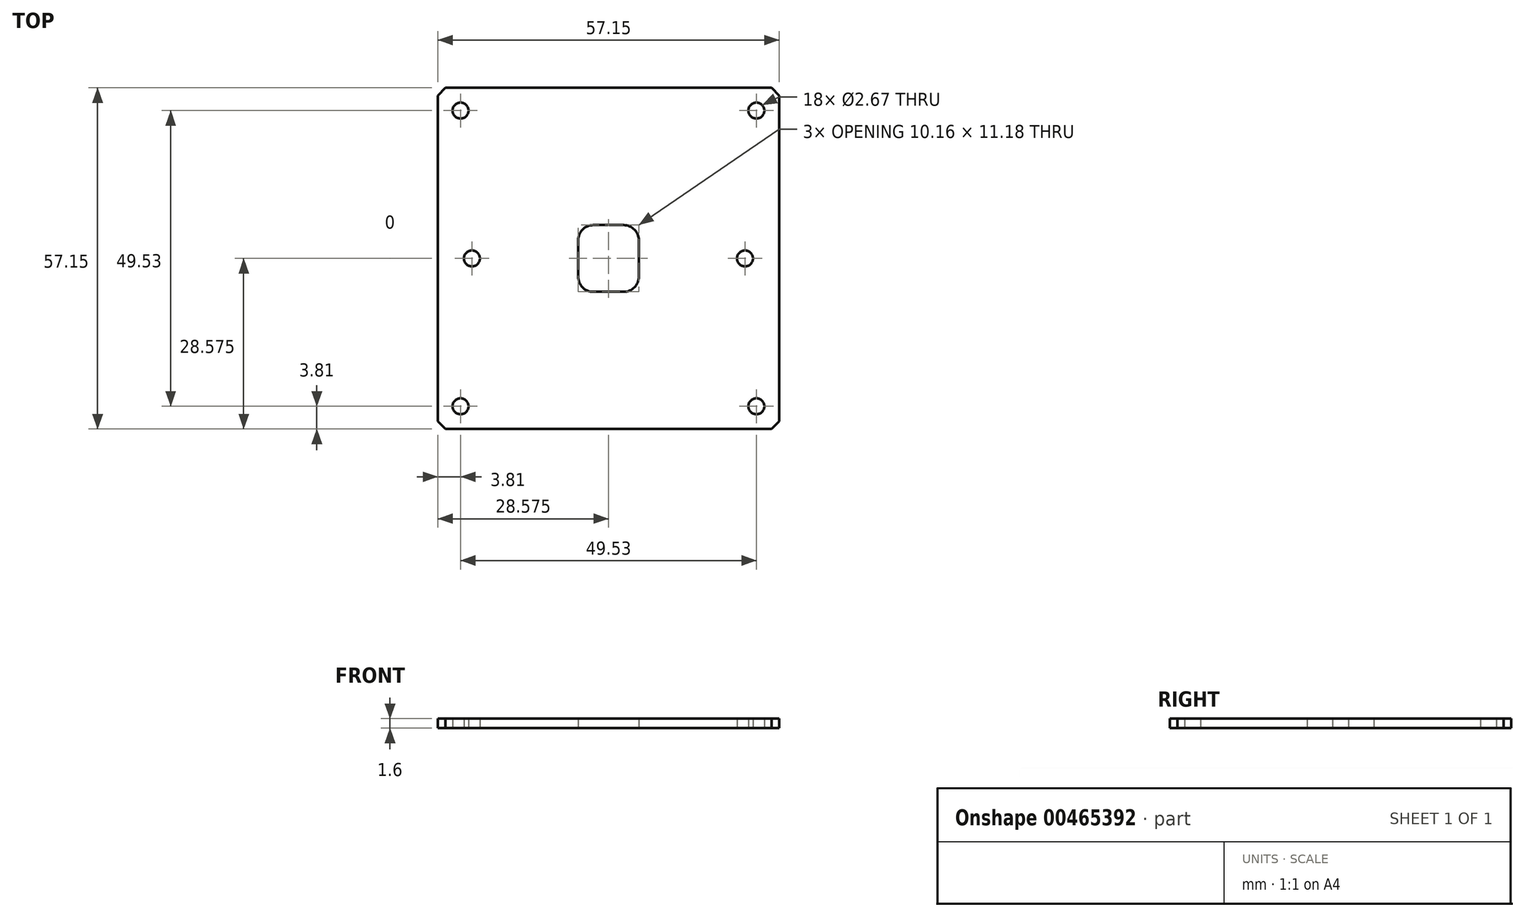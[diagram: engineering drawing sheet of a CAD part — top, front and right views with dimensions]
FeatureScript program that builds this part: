
annotation { "Feature Type Name" : "Feature", "Feature Type Description" : "" }
export const myFeature = defineFeature(function(context is Context, id is Id, definition is map)
    precondition{}
    {
        {
            var Q0;
            Q0=qCreatedBy(makeId("Top.planeOp"),FACE);
            var sketch = newSketch(context, id + "F0", { "sketchPlane" : qUnion([Q0])});
            skLineSegment(sketch, "E0.bottom", {"start": v(0, 0) * mm, "end": v(57.15, 0) * mm});
            skLineSegment(sketch, "E0.top", {"start": v(0, -57.15) * mm, "end": v(57.15, -57.15) * mm});
            skLineSegment(sketch, "E0.left", {"start": v(0, 0) * mm, "end": v(0, -57.15) * mm});
            skLineSegment(sketch, "E0.right", {"start": v(57.15, 0) * mm, "end": v(57.15, -57.15) * mm});
            skCircle(sketch, "E1", {"center": v(53.34, -3.8) * mm, "radius": 1.33 * mm});
            skLineSegment(sketch, "E2", {"start": v(57.15, -28.58) * mm, "end": v(0, -28.58) * mm, "construction": true});
            skLineSegment(sketch, "E3", {"start": v(28.58, 0) * mm, "end": v(28.58, -57.15) * mm, "construction": true});
            skLineSegment(sketch, "E4", {"start": v(55.87, 0) * mm, "end": v(57.15, -1.28) * mm});
            skCircle(sketch, "E5.MirrorC", {"center": v(53.34, -53.34) * mm, "radius": 1.33 * mm});
            skLineSegment(sketch, "E6.MirrorCS", {"start": v(55.87, -57.15) * mm, "end": v(57.15, -55.87) * mm});
            skCircle(sketch, "E7.MirrorC", {"center": v(3.81, -53.34) * mm, "radius": 1.33 * mm});
            skCircle(sketch, "E8.MirrorC", {"center": v(3.81, -3.8) * mm, "radius": 1.33 * mm});
            skLineSegment(sketch, "E9.MirrorCS", {"start": v(1.28, -57.15) * mm, "end": v(0, -55.87) * mm});
            skLineSegment(sketch, "E10.MirrorCS", {"start": v(1.28, 0) * mm, "end": v(0, -1.28) * mm});
            skCircle(sketch, "E11", {"center": v(51.44, -28.57) * mm, "radius": 1.33 * mm});
            skCircle(sketch, "E12.MirrorC", {"center": v(5.72, -28.57) * mm, "radius": 1.33 * mm});
            skLineSegment(sketch, "E13.bottom", {"start": v(26.04, -22.99) * mm, "end": v(31.11, -22.99) * mm});
            skLineSegment(sketch, "E13.top", {"start": v(26.04, -34.16) * mm, "end": v(31.12, -34.16) * mm});
            skLineSegment(sketch, "E13.left", {"start": v(23.5, -25.53) * mm, "end": v(23.5, -31.62) * mm});
            skLineSegment(sketch, "E13.right", {"start": v(33.65, -25.53) * mm, "end": v(33.65, -31.62) * mm});
            skPoint(sketch, "E14", {"position": v(28.58, -22.99) * mm});
            skPoint(sketch, "E15", {"position": v(33.65, -28.57) * mm});
            skPoint(sketch, "E16.visualSharp", {"position": v(33.66, -22.99) * mm});
            skArc(sketch, "E16.filletArc", {"start": v(33.65, -25.53) * mm, "mid": v(32.91, -23.73) * mm, "end": v(31.11, -22.99) * mm});
            skPoint(sketch, "E17.visualSharp", {"position": v(23.5, -22.99) * mm});
            skArc(sketch, "E17.filletArc", {"start": v(26.04, -22.99) * mm, "mid": v(24.24, -23.73) * mm, "end": v(23.5, -25.53) * mm});
            skPoint(sketch, "E18.visualSharp", {"position": v(33.66, -34.16) * mm});
            skArc(sketch, "E18.filletArc", {"start": v(31.12, -34.16) * mm, "mid": v(32.91, -33.42) * mm, "end": v(33.66, -31.62) * mm});
            skPoint(sketch, "E19.visualSharp", {"position": v(23.5, -34.16) * mm});
            skArc(sketch, "E19.filletArc", {"start": v(23.5, -31.62) * mm, "mid": v(24.24, -33.42) * mm, "end": v(26.04, -34.16) * mm});
            skSolve(sketch);
        }
        {
            var Q0;
            Q0=makeQuery(id+"F0.imprint","IMPRINT",FACE,{"disambiguationData":[TD([[makeQuery(id+"F0.imprint","IMPRINT",EDGE,{"derivedFrom":sQuery(id+"F0.wireOp",EDGE,"E1")}),-1.0]])]});
            extrude(context, id + "F1", {"entities" : qUnion([Q0]), "depth" : 1.6 * mm, "offsetDistance" : 25 * mm});
        }
        {
            var Q0;
            Q0=makeQuery(id+"F1.opExtrude","CAP_FACE",FACE,{"disambiguationData":[OSD([sQuery(id+"F0.wireOp",EDGE,"E0.bottom"),sQuery(id+"F0.wireOp",EDGE,"E0.top"),sQuery(id+"F0.wireOp",EDGE,"E0.left"),sQuery(id+"F0.wireOp",EDGE,"E0.right"),sQuery(id+"F0.wireOp",EDGE,"E1"),sQuery(id+"F0.wireOp",EDGE,"E4"),sQuery(id+"F0.wireOp",EDGE,"E5.MirrorC"),sQuery(id+"F0.wireOp",EDGE,"E6.MirrorCS"),sQuery(id+"F0.wireOp",EDGE,"E7.MirrorC"),sQuery(id+"F0.wireOp",EDGE,"E8.MirrorC"),sQuery(id+"F0.wireOp",EDGE,"E9.MirrorCS"),sQuery(id+"F0.wireOp",EDGE,"E10.MirrorCS")])],"isStart":false});
            var sketch = newSketch(context, id + "F2", { "sketchPlane" : qUnion([Q0])});
            skLineSegment(sketch, "E20", {"start": v(28.58, -57.15) * mm, "end": v(28.58, 0) * mm, "construction": true});
            skPoint(sketch, "E21", {"position": v(28.58, -50.8) * mm});
            skPoint(sketch, "E22", {"position": v(28.58, -6.35) * mm});
            skSolve(sketch);
        }
        {
            var Q0;
            Q0=makeQuery(id+"F1.opExtrude","CAP_FACE",FACE,{"disambiguationData":[OSD([sQuery(id+"F0.wireOp",EDGE,"E0.bottom"),sQuery(id+"F0.wireOp",EDGE,"E0.top"),sQuery(id+"F0.wireOp",EDGE,"E0.left"),sQuery(id+"F0.wireOp",EDGE,"E0.right"),sQuery(id+"F0.wireOp",EDGE,"E1"),sQuery(id+"F0.wireOp",EDGE,"E4"),sQuery(id+"F0.wireOp",EDGE,"E5.MirrorC"),sQuery(id+"F0.wireOp",EDGE,"E6.MirrorCS"),sQuery(id+"F0.wireOp",EDGE,"E7.MirrorC"),sQuery(id+"F0.wireOp",EDGE,"E8.MirrorC"),sQuery(id+"F0.wireOp",EDGE,"E9.MirrorCS"),sQuery(id+"F0.wireOp",EDGE,"E10.MirrorCS")])],"isStart":true});
            var sketch = newSketch(context, id + "F3", { "sketchPlane" : qUnion([Q0])});
            skLineSegment(sketch, "E23", {"start": v(0, 28.58) * mm, "end": v(57.15, 28.58) * mm, "construction": true});
            skPoint(sketch, "E24", {"position": v(6.35, 28.58) * mm});
            skPoint(sketch, "E25", {"position": v(50.8, 28.58) * mm});
            skSolve(sketch);
        }
    });
